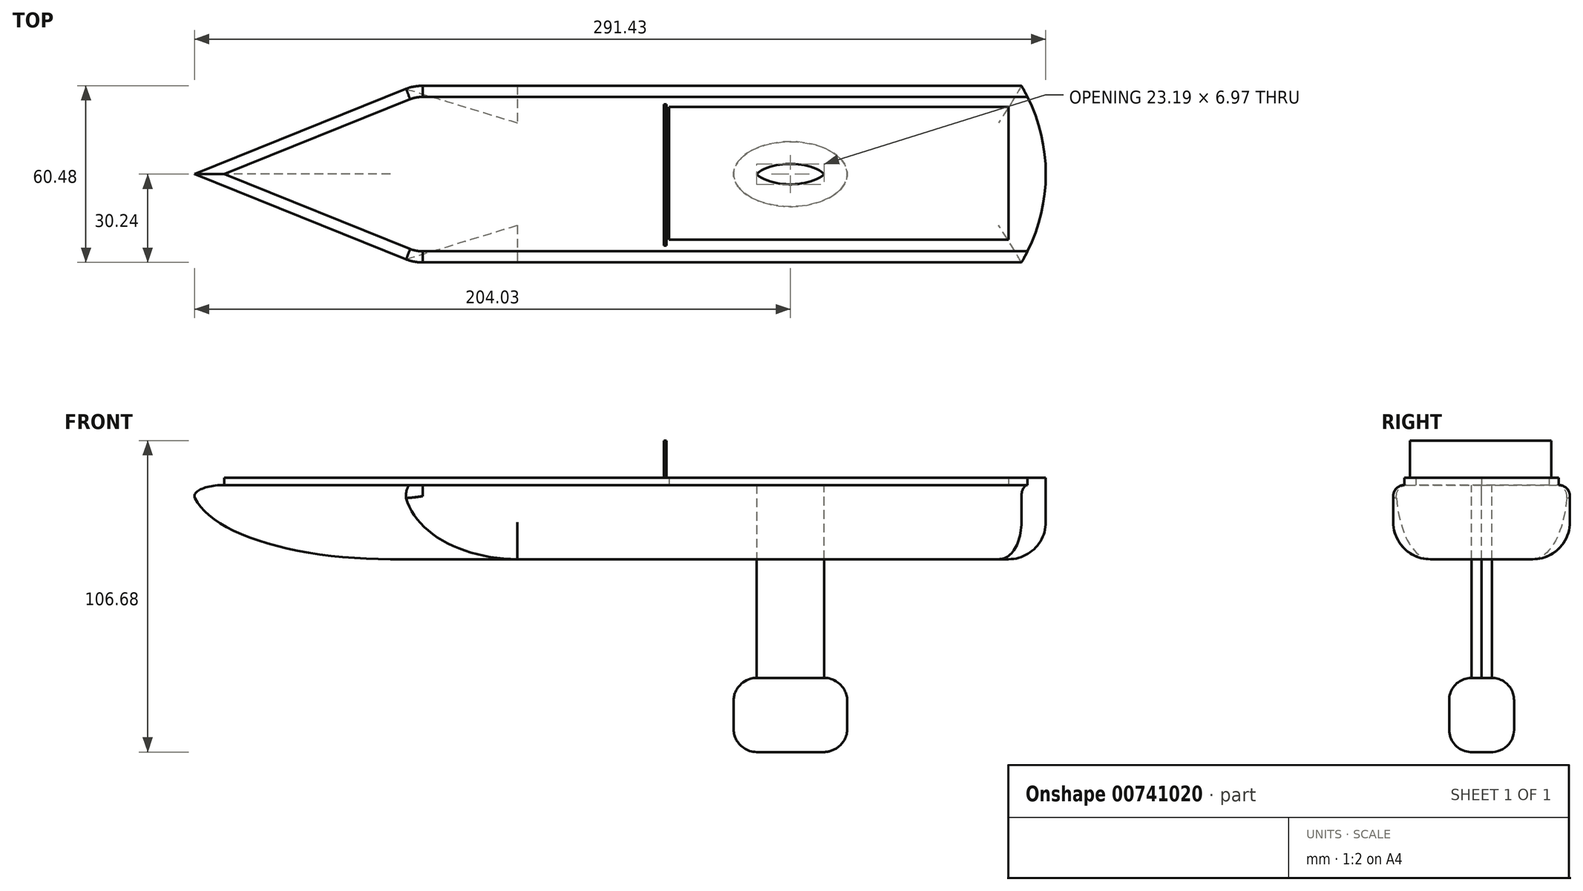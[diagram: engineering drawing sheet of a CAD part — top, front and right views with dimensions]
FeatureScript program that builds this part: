
annotation { "Feature Type Name" : "Feature", "Feature Type Description" : "" }
export const myFeature = defineFeature(function(context is Context, id is Id, definition is map)
    precondition{}
    {
        {
            var Q0;
            Q0=qCreatedBy(makeId("Top.planeOp"),FACE);
            var sketch = newSketch(context, id + "F0", { "sketchPlane" : qUnion([Q0])});
            skEllipse(sketch, "E0", {"center": v(0, 0) * mm, "majorRadius": 19.43 * mm, "minorRadius": 11.1 * mm, "majorAxis": v(-1, 0)});
            skSolve(sketch);
        }
        {
            var Q0;
            Q0=makeQuery(id+"F0.imprint","IMPRINT",FACE,{"disambiguationData":[TD([[makeQuery(id+"F0.imprint","IMPRINT",EDGE,{"derivedFrom":sQuery(id+"F0.wireOp",EDGE,"E0")}),1.0]])]});
            extrude(context, id + "F1", {"entities" : qUnion([Q0]), "depth" : 25.4 * mm, "offsetDistance" : 25.4 * mm});
        }
        {
            var Q0;
            Q0=makeQuery(id+"F1.opExtrude","CAP_EDGE",EDGE,{"disambiguationData":[OSD([sQuery(id+"F0.wireOp",EDGE,"E0")])],"isStart":false});
            var Q1;
            Q1=makeQuery(id+"F1.opExtrude","CAP_EDGE",EDGE,{"disambiguationData":[OSD([sQuery(id+"F0.wireOp",EDGE,"E0")])],"isStart":true});
            fillet(context, id + "F2", {"entities" : qUnion([Q0, Q1]), "radius" : 7.62 * mm, "tangentPropagation" : true, "allowEdgeOverflow" : false});
        }
        {
            var Q0;
            Q0=makeQuery(id+"F1.opExtrude","CAP_FACE",FACE,{"disambiguationData":[OSD([sQuery(id+"F0.wireOp",EDGE,"E0")])],"isStart":false});
            extrude(context, id + "F3", {"entities" : qUnion([Q0]), "operationType" : NewBodyOperationType.ADD, "depth" : 40.64 * mm, "offsetDistance" : 25.4 * mm});
        }
        {
            var Q0;
            Q0=makeQuery(id+"F3.opExtrude","CAP_FACE",FACE,{"disambiguationData":[OSD([sQuery(id+"F0.wireOp",EDGE,"E0")])],"isStart":false});
            var sketch = newSketch(context, id + "F4", { "sketchPlane" : qUnion([Q0])});
            skLineSegment(sketch, "E1.bottom", {"start": v(-79.09, -30.24) * mm, "end": v(79.09, -30.24) * mm});
            skLineSegment(sketch, "E1.top", {"start": v(-79.09, 30.24) * mm, "end": v(79.09, 30.24) * mm});
            skLineSegment(sketch, "E1.left", {"start": v(-79.09, -30.24) * mm, "end": v(-79.09, 30.24) * mm});
            skLineSegment(sketch, "E1.right", {"start": v(79.09, -30.24) * mm, "end": v(79.09, 30.24) * mm});
            skPoint(sketch, "E1.middle", {"position": v(0, 0) * mm});
            skSolve(sketch);
        }
        {
            var Q0;
            Q0=makeQuery(id+"F4.imprint","IMPRINT",FACE,{"disambiguationData":[TD([[makeQuery(id+"F4.imprint","IMPRINT",EDGE,{"derivedFrom":sQuery(id+"F4.wireOp",EDGE,"E1.bottom")}),1.0]])]});
            extrude(context, id + "F5", {"entities" : qUnion([Q0]), "depth" : 25.4 * mm, "offsetDistance" : 25.4 * mm});
        }
        {
            var Q0;
            Q0=makeQuery(id+"F5.opExtrude","SWEPT_FACE",FACE,{"disambiguationData":[OSD([sQuery(id+"F4.wireOp",EDGE,"E1.left")])]});
            extrude(context, id + "F6", {"entities" : qUnion([Q0]), "operationType" : NewBodyOperationType.ADD, "depth" : 50.8 * mm, "offsetDistance" : 25.4 * mm});
        }
        {
            var Q0;
            {var subQ0=sQuery(id+"F4.wireOp",EDGE,"E1.left");Q0=makeQuery(id+"F6.boolean.opBoolean","MERGE",FACE,{"derivedFrom":[makeQuery(id+"F5.opExtrude","CAP_FACE",FACE,{"disambiguationData":[OSD([sQuery(id+"F0.wireOp",EDGE,"E0"),sQuery(id+"F4.wireOp",EDGE,"E1.bottom"),sQuery(id+"F4.wireOp",EDGE,"E1.top"),subQ0,sQuery(id+"F4.wireOp",EDGE,"E1.right")])],"isStart":false}),makeQuery(id+"F6.opExtrude","SWEPT_FACE",FACE,{"disambiguationData":[OSD([subQ0]),TDD([makeQuery(id+"F5.opExtrude","CAP_EDGE",EDGE,{"disambiguationData":[OSD([subQ0])],"isStart":false})])]})]});}
            var sketch = newSketch(context, id + "F7", { "sketchPlane" : qUnion([Q0])});
            skLineSegment(sketch, "E2", {"start": v(-129.89, 30.24) * mm, "end": v(-204.94, 0) * mm});
            skPoint(sketch, "E2.endSnap0", {"position": v(-129.89, 0) * mm});
            skLineSegment(sketch, "E3", {"start": v(-204.94, 0) * mm, "end": v(-129.89, -30.24) * mm});
            skSolve(sketch);
        }
        {
            var Q0;
            Q0=makeQuery(id+"F7.imprint","IMPRINT",FACE,{"disambiguationData":[TD([[makeQuery(id+"F7.imprint","IMPRINT",EDGE,{"derivedFrom":sQuery(id+"F7.wireOp",EDGE,"E2")}),1.0]])]});
            extrude(context, id + "F8", {"entities" : qUnion([Q0]), "operationType" : NewBodyOperationType.ADD, "depth" : -25.4 * mm, "offsetDistance" : 25.4 * mm});
        }
        {
            var Q0;
            Q0=makeQuery(id+"F8.opExtrude","CAP_EDGE",EDGE,{"disambiguationData":[OSD([sQuery(id+"F7.wireOp",EDGE,"E2")])],"isStart":false});
            var Q1;
            Q1=makeQuery(id+"F8.opExtrude","CAP_EDGE",EDGE,{"disambiguationData":[OSD([sQuery(id+"F7.wireOp",EDGE,"E3")])],"isStart":false});
            fillet(context, id + "F9", {"entities" : qUnion([Q0, Q1]), "radius" : 25.4 * mm, "tangentPropagation" : true, "allowEdgeOverflow" : false});
        }
        {
            var Q0;
            {var subQ0=sQuery(id+"F4.wireOp",EDGE,"E1.left");var subQ1=sQuery(id+"F4.wireOp",EDGE,"E1.bottom");Q0=makeQuery(id+"F6.boolean.opBoolean","MERGE",EDGE,{"derivedFrom":[makeQuery(id+"F5.opExtrude","CAP_EDGE",EDGE,{"disambiguationData":[OSD([subQ1])],"isStart":true}),makeQuery(id+"F6.opExtrude","SWEPT_EDGE",EDGE,{"disambiguationData":[OSD([subQ1,subQ0]),TDD([makeQuery(id+"F5.opExtrude","CAP_VERTEX",VERTEX,{"disambiguationData":[OSD([subQ1,subQ0])],"isStart":true})])]})]});}
            var Q1;
            {var subQ0=sQuery(id+"F4.wireOp",EDGE,"E1.left");var subQ1=sQuery(id+"F4.wireOp",EDGE,"E1.top");Q1=makeQuery(id+"F6.boolean.opBoolean","MERGE",EDGE,{"derivedFrom":[makeQuery(id+"F5.opExtrude","CAP_EDGE",EDGE,{"disambiguationData":[OSD([subQ1])],"isStart":true}),makeQuery(id+"F6.opExtrude","SWEPT_EDGE",EDGE,{"disambiguationData":[OSD([subQ1,subQ0]),TDD([makeQuery(id+"F5.opExtrude","CAP_VERTEX",VERTEX,{"disambiguationData":[OSD([subQ1,subQ0])],"isStart":true})])]})]});}
            fillet(context, id + "F10", {"entities" : qUnion([Q0, Q1]), "radius" : 12.7 * mm, "tangentPropagation" : true, "allowEdgeOverflow" : false});
        }
        {
            var Q0;
            {var subQ0=sQuery(id+"F4.wireOp",EDGE,"E1.left");Q0=makeQuery(id+"F8.boolean.opBoolean","MERGE",FACE,{"derivedFrom":[makeQuery(id+"F6.boolean.opBoolean","MERGE",FACE,{"derivedFrom":[makeQuery(id+"F5.opExtrude","CAP_FACE",FACE,{"disambiguationData":[OSD([sQuery(id+"F0.wireOp",EDGE,"E0"),sQuery(id+"F4.wireOp",EDGE,"E1.bottom"),sQuery(id+"F4.wireOp",EDGE,"E1.top"),subQ0,sQuery(id+"F4.wireOp",EDGE,"E1.right")])],"isStart":false}),makeQuery(id+"F6.opExtrude","SWEPT_FACE",FACE,{"disambiguationData":[OSD([subQ0]),TDD([makeQuery(id+"F5.opExtrude","CAP_EDGE",EDGE,{"disambiguationData":[OSD([subQ0])],"isStart":false})])]})]}),makeQuery(id+"F8.opExtrude","CAP_FACE",FACE,{"disambiguationData":[OSD([subQ0,sQuery(id+"F7.wireOp",EDGE,"E2"),sQuery(id+"F7.wireOp",EDGE,"E3")])],"isStart":true})]});}
            var sketch = newSketch(context, id + "F11", { "sketchPlane" : qUnion([Q0])});
            skArc(sketch, "E4", {"start": v(79.09, -30.24) * mm, "mid": v(87.4, 0) * mm, "end": v(79.09, 30.24) * mm});
            skSolve(sketch);
        }
        {
            var Q0;
            Q0=makeQuery(id+"F11.imprint","IMPRINT",FACE,{"disambiguationData":[TD([[makeQuery(id+"F11.imprint","IMPRINT",EDGE,{"derivedFrom":sQuery(id+"F11.wireOp",EDGE,"E4")}),1.0]])]});
            extrude(context, id + "F12", {"entities" : qUnion([Q0]), "operationType" : NewBodyOperationType.ADD, "depth" : -25.4 * mm, "offsetDistance" : 25.4 * mm});
        }
        {
            var Q0;
            Q0=makeQuery(id+"F12.opExtrude","CAP_EDGE",EDGE,{"disambiguationData":[OSD([sQuery(id+"F11.wireOp",EDGE,"E4")])],"isStart":false});
            fillet(context, id + "F13", {"entities" : qUnion([Q0]), "radius" : 12.7 * mm, "tangentPropagation" : true, "allowEdgeOverflow" : false});
        }
        {
            var Q0;
            {var subQ0=sQuery(id+"F7.wireOp",EDGE,"E3");var subQ1=sQuery(id+"F4.wireOp",EDGE,"E1.left");Q0=makeQuery(id+"F9.opFillet","BLEND_EDGE",EDGE,{"blendedFrom":[makeQuery(id+"F8.opExtrude","CAP_EDGE",EDGE,{"disambiguationData":[OSD([subQ0])],"isStart":false}),makeQuery(id+"F8.boolean.opBoolean","MERGE",FACE,{"derivedFrom":[makeQuery(id+"F6.boolean.opBoolean","MERGE",FACE,{"derivedFrom":[makeQuery(id+"F5.opExtrude","CAP_FACE",FACE,{"disambiguationData":[OSD([sQuery(id+"F0.wireOp",EDGE,"E0"),sQuery(id+"F4.wireOp",EDGE,"E1.bottom"),sQuery(id+"F4.wireOp",EDGE,"E1.top"),subQ1,sQuery(id+"F4.wireOp",EDGE,"E1.right")])],"isStart":false}),makeQuery(id+"F6.opExtrude","SWEPT_FACE",FACE,{"disambiguationData":[OSD([subQ1]),TDD([makeQuery(id+"F5.opExtrude","CAP_EDGE",EDGE,{"disambiguationData":[OSD([subQ1])],"isStart":false})])]})]}),makeQuery(id+"F8.opExtrude","CAP_FACE",FACE,{"disambiguationData":[OSD([subQ1,sQuery(id+"F7.wireOp",EDGE,"E2"),subQ0])],"isStart":true})]})],"blendedInto":[makeQuery(id+"F8.boolean.opBoolean","MERGE",FACE,{"derivedFrom":[makeQuery(id+"F6.boolean.opBoolean","MERGE",FACE,{"derivedFrom":[makeQuery(id+"F5.opExtrude","CAP_FACE",FACE,{"disambiguationData":[OSD([sQuery(id+"F0.wireOp",EDGE,"E0"),sQuery(id+"F4.wireOp",EDGE,"E1.bottom"),sQuery(id+"F4.wireOp",EDGE,"E1.top"),subQ1,sQuery(id+"F4.wireOp",EDGE,"E1.right")])],"isStart":false}),makeQuery(id+"F6.opExtrude","SWEPT_FACE",FACE,{"disambiguationData":[OSD([subQ1]),TDD([makeQuery(id+"F5.opExtrude","CAP_EDGE",EDGE,{"disambiguationData":[OSD([subQ1])],"isStart":false})])]})]}),makeQuery(id+"F8.opExtrude","CAP_FACE",FACE,{"disambiguationData":[OSD([subQ1,sQuery(id+"F7.wireOp",EDGE,"E2"),subQ0])],"isStart":true})]})]});}
            var Q1;
            {var subQ0=sQuery(id+"F7.wireOp",EDGE,"E2");var subQ1=sQuery(id+"F4.wireOp",EDGE,"E1.left");Q1=makeQuery(id+"F9.opFillet","BLEND_EDGE",EDGE,{"blendedFrom":[makeQuery(id+"F8.opExtrude","CAP_EDGE",EDGE,{"disambiguationData":[OSD([subQ0])],"isStart":false}),makeQuery(id+"F8.boolean.opBoolean","MERGE",FACE,{"derivedFrom":[makeQuery(id+"F6.boolean.opBoolean","MERGE",FACE,{"derivedFrom":[makeQuery(id+"F5.opExtrude","CAP_FACE",FACE,{"disambiguationData":[OSD([sQuery(id+"F0.wireOp",EDGE,"E0"),sQuery(id+"F4.wireOp",EDGE,"E1.bottom"),sQuery(id+"F4.wireOp",EDGE,"E1.top"),subQ1,sQuery(id+"F4.wireOp",EDGE,"E1.right")])],"isStart":false}),makeQuery(id+"F6.opExtrude","SWEPT_FACE",FACE,{"disambiguationData":[OSD([subQ1]),TDD([makeQuery(id+"F5.opExtrude","CAP_EDGE",EDGE,{"disambiguationData":[OSD([subQ1])],"isStart":false})])]})]}),makeQuery(id+"F8.opExtrude","CAP_FACE",FACE,{"disambiguationData":[OSD([subQ1,subQ0,sQuery(id+"F7.wireOp",EDGE,"E3")])],"isStart":true})]})],"blendedInto":[makeQuery(id+"F8.boolean.opBoolean","MERGE",FACE,{"derivedFrom":[makeQuery(id+"F6.boolean.opBoolean","MERGE",FACE,{"derivedFrom":[makeQuery(id+"F5.opExtrude","CAP_FACE",FACE,{"disambiguationData":[OSD([sQuery(id+"F0.wireOp",EDGE,"E0"),sQuery(id+"F4.wireOp",EDGE,"E1.bottom"),sQuery(id+"F4.wireOp",EDGE,"E1.top"),subQ1,sQuery(id+"F4.wireOp",EDGE,"E1.right")])],"isStart":false}),makeQuery(id+"F6.opExtrude","SWEPT_FACE",FACE,{"disambiguationData":[OSD([subQ1]),TDD([makeQuery(id+"F5.opExtrude","CAP_EDGE",EDGE,{"disambiguationData":[OSD([subQ1])],"isStart":false})])]})]}),makeQuery(id+"F8.opExtrude","CAP_FACE",FACE,{"disambiguationData":[OSD([subQ1,subQ0,sQuery(id+"F7.wireOp",EDGE,"E3")])],"isStart":true})]})]});}
            fillet(context, id + "F14", {"entities" : qUnion([Q0, Q1]), "radius" : 3.8 * mm, "tangentPropagation" : true, "allowEdgeOverflow" : false});
        }
        {
            var Q0;
            {var subQ0=sQuery(id+"F4.wireOp",EDGE,"E1.right");var subQ1=sQuery(id+"F4.wireOp",EDGE,"E1.left");Q0=makeQuery(id+"F12.boolean.opBoolean","MERGE",FACE,{"derivedFrom":[makeQuery(id+"F8.boolean.opBoolean","MERGE",FACE,{"derivedFrom":[makeQuery(id+"F6.boolean.opBoolean","MERGE",FACE,{"derivedFrom":[makeQuery(id+"F5.opExtrude","CAP_FACE",FACE,{"disambiguationData":[OSD([sQuery(id+"F0.wireOp",EDGE,"E0"),sQuery(id+"F4.wireOp",EDGE,"E1.bottom"),sQuery(id+"F4.wireOp",EDGE,"E1.top"),subQ1,subQ0])],"isStart":false}),makeQuery(id+"F6.opExtrude","SWEPT_FACE",FACE,{"disambiguationData":[OSD([subQ1]),TDD([makeQuery(id+"F5.opExtrude","CAP_EDGE",EDGE,{"disambiguationData":[OSD([subQ1])],"isStart":false})])]})]}),makeQuery(id+"F8.opExtrude","CAP_FACE",FACE,{"disambiguationData":[OSD([subQ1,sQuery(id+"F7.wireOp",EDGE,"E2"),sQuery(id+"F7.wireOp",EDGE,"E3")])],"isStart":true})]}),makeQuery(id+"F12.opExtrude","CAP_FACE",FACE,{"disambiguationData":[OSD([subQ0,sQuery(id+"F11.wireOp",EDGE,"E4")])],"isStart":true})]});}
            var sketch = newSketch(context, id + "F15", { "sketchPlane" : qUnion([Q0])});
            skLineSegment(sketch, "E5.bottom", {"start": v(-41.53, 23.05) * mm, "end": v(74.62, 23.05) * mm});
            skLineSegment(sketch, "E5.top", {"start": v(-41.53, -22.46) * mm, "end": v(74.62, -22.46) * mm});
            skLineSegment(sketch, "E5.left", {"start": v(-41.53, 23.05) * mm, "end": v(-41.53, -22.46) * mm});
            skLineSegment(sketch, "E5.right", {"start": v(74.62, 23.05) * mm, "end": v(74.62, -22.46) * mm});
            skSolve(sketch);
        }
        {
            var Q0;
            Q0=makeQuery(id+"F15.imprint","IMPRINT",FACE,{"disambiguationData":[TD([[makeQuery(id+"F15.imprint","IMPRINT",EDGE,{"derivedFrom":sQuery(id+"F15.wireOp",EDGE,"E5.bottom")}),1.0]])]});
            extrude(context, id + "F16", {"entities" : qUnion([Q0]), "operationType" : NewBodyOperationType.ADD, "depth" : 2.54 * mm, "offsetDistance" : 25.4 * mm});
        }
        {
            var Q0;
            Q0=makeQuery(id+"F16.opExtrude","CAP_FACE",FACE,{"disambiguationData":[OSD([sQuery(id+"F0.wireOp",EDGE,"E0"),sQuery(id+"F4.wireOp",EDGE,"E1.bottom"),sQuery(id+"F4.wireOp",EDGE,"E1.top"),sQuery(id+"F4.wireOp",EDGE,"E1.left"),sQuery(id+"F4.wireOp",EDGE,"E1.right"),sQuery(id+"F7.wireOp",EDGE,"E2"),sQuery(id+"F7.wireOp",EDGE,"E3"),sQuery(id+"F11.wireOp",EDGE,"E4"),sQuery(id+"F15.wireOp",EDGE,"E5.bottom"),sQuery(id+"F15.wireOp",EDGE,"E5.top"),sQuery(id+"F15.wireOp",EDGE,"E5.left"),sQuery(id+"F15.wireOp",EDGE,"E5.right")])],"isStart":false});
            var sketch = newSketch(context, id + "F17", { "sketchPlane" : qUnion([Q0])});
            skLineSegment(sketch, "E6", {"start": v(-43.98, -26.43) * mm, "end": v(-43.98, 26.43) * mm});
            skSolve(sketch);
        }
        {
            var Q0;
            {var subQ11=sQuery(id+"F17.wireOp",EDGE,"E6");Q0=makeQuery(id+"F17.imprint","IMPRINT",FACE,{"disambiguationData":[TD([[makeQuery(id+"F17.imprint","IMPRINT",EDGE,{"derivedFrom":subQ11}),-1.0]])]});}
            var sketch = newSketch(context, id + "F18", { "sketchPlane" : qUnion([Q0])});
            skLineSegment(sketch, "E7.bottom", {"start": v(-42.48, -24.51) * mm, "end": v(-43.26, -24.51) * mm});
            skLineSegment(sketch, "E7.top", {"start": v(-42.48, 23.86) * mm, "end": v(-43.26, 23.86) * mm});
            skLineSegment(sketch, "E7.left", {"start": v(-42.48, -24.51) * mm, "end": v(-42.48, 23.86) * mm});
            skLineSegment(sketch, "E7.right", {"start": v(-43.26, -24.51) * mm, "end": v(-43.26, 23.86) * mm});
            skSolve(sketch);
        }
        {
            var Q0;
            Q0=makeQuery(id+"F18.imprint","IMPRINT",FACE,{"disambiguationData":[TD([[makeQuery(id+"F18.imprint","IMPRINT",EDGE,{"derivedFrom":sQuery(id+"F18.wireOp",EDGE,"E7.bottom")}),1.0]])]});
            var sketch = newSketch(context, id + "F19", { "sketchPlane" : qUnion([Q0])});
            skSolve(sketch);
        }
        {
            var Q0;
            Q0=makeQuery(id+"F19.imprint","IMPRINT",FACE,{"disambiguationData":[TD([[makeQuery(id+"F19.imprint","IMPRINT",EDGE,{"derivedFrom":makeQuery(id+"F18.imprint","IMPRINT",EDGE,{"derivedFrom":sQuery(id+"F18.wireOp",EDGE,"E7.bottom")})}),-1.0]])]});
            extrude(context, id + "F20", {"entities" : qUnion([Q0]), "operationType" : NewBodyOperationType.ADD, "depth" : 12.7 * mm, "offsetDistance" : 25.4 * mm});
        }
    });
